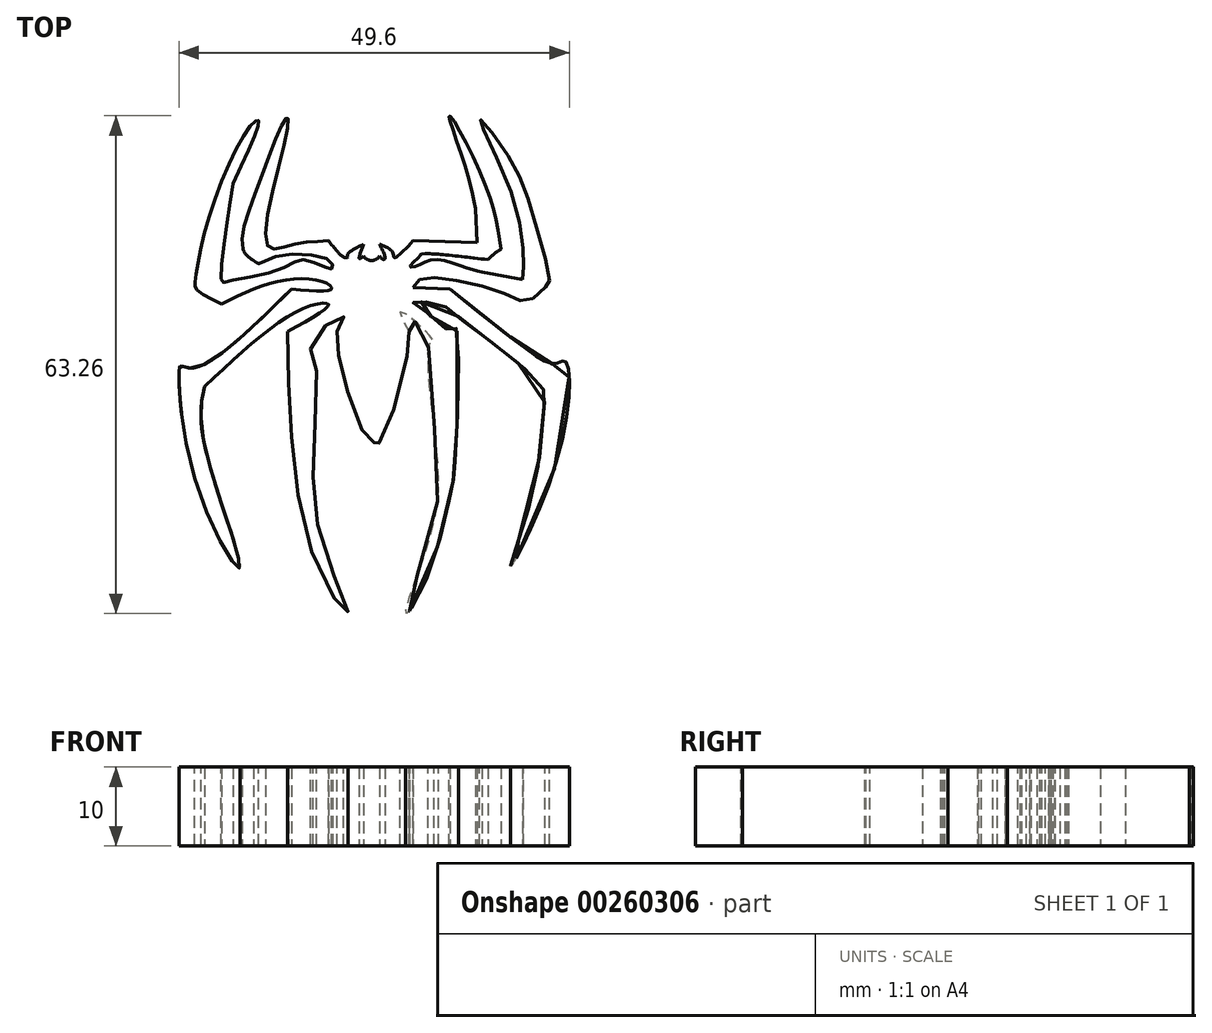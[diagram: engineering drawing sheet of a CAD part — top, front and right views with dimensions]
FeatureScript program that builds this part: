
annotation { "Feature Type Name" : "Feature", "Feature Type Description" : "" }
export const myFeature = defineFeature(function(context is Context, id is Id, definition is map)
    precondition{}
    {
        {
            var Q0;
            Q0=qCreatedBy(makeId("Top.planeOp"),FACE);
            var sketch = newSketch(context, id + "F0", { "sketchPlane" : qUnion([Q0])});
            skFitSpline(sketch, "E0", {"points": [v(26.14, 47.25) * mm, v(26.81, 45.39) * mm, v(26.49, 45.37) * mm, v(26.16, 45.74) * mm], "startDerivative": vector(2.32, -4.7) * mm, "endDerivative": vector(-1.04, 1.72) * mm});
            skFitSpline(sketch, "E1", {"points": [v(26.16, 45.74) * mm, v(25.6, 45.28) * mm, v(24.59, 45.3) * mm, v(24.1, 45.74) * mm], "startDerivative": vector(-1.46, -1.71) * mm, "endDerivative": vector(-1.26, 1.71) * mm});
            skFitSpline(sketch, "E2", {"points": [v(24.1, 45.74) * mm, v(23.56, 45.42) * mm, v(24.1, 47.25) * mm], "startDerivative": vector(-1.93, -1.58) * mm, "endDerivative": vector(1.61, 4.08) * mm});
            skFitSpline(sketch, "E3", {"points": [v(24.1, 47.25) * mm, v(22.13, 46.05) * mm, v(22.1, 45.6) * mm], "startDerivative": vector(-3.83, -1.81) * mm, "endDerivative": vector(0.37, -1.42) * mm});
            skFitSpline(sketch, "E4", {"points": [v(26.14, 47.25) * mm, v(27.79, 46.24) * mm, v(28, 45.57) * mm, v(30.4, 47.7) * mm], "startDerivative": vector(6.19, -2.42) * mm, "endDerivative": vector(7.2, 7.58) * mm});
            skFitSpline(sketch, "E5", {"points": [v(22.1, 45.6) * mm, v(21.6, 45.6) * mm, v(19.65, 47.7) * mm], "startDerivative": vector(-1.58, -0.44) * mm, "endDerivative": vector(-3.12, 4.02) * mm});
            skFitSpline(sketch, "E6", {"points": [v(30.4, 47.7) * mm, v(38.5, 47.45) * mm], "startDerivative": vector(8.09, -0.25) * mm, "endDerivative": vector(8.09, -0.25) * mm});
            skFitSpline(sketch, "E7", {"points": [v(38.5, 47.45) * mm, v(38.31, 51.77) * mm], "startDerivative": vector(-0.18, 4.33) * mm, "endDerivative": vector(-0.18, 4.33) * mm});
            skFitSpline(sketch, "E8", {"points": [v(38.31, 51.77) * mm, v(37.02, 57.13) * mm, v(35, 63.59) * mm, v(39.43, 55.13) * mm, v(41.56, 46.66) * mm], "startDerivative": vector(-3.78, 20.99) * mm, "endDerivative": vector(3.96, -27.47) * mm});
            skFitSpline(sketch, "E9", {"points": [v(41.56, 46.66) * mm, v(40.56, 45.93) * mm, v(39.9, 45.3) * mm], "startDerivative": vector(-1.98, -1.35) * mm, "endDerivative": vector(-1.33, -1.36) * mm});
            skFitSpline(sketch, "E10", {"points": [v(39.9, 45.3) * mm, v(31.39, 46) * mm, v(31.24, 45.74) * mm, v(30, 44.48) * mm, v(30.73, 44.43) * mm, v(33.04, 45.3) * mm, v(37.2, 44.25) * mm, v(39.13, 43.74) * mm], "startDerivative": vector(-44.14, 5.21) * mm, "endDerivative": vector(12.78, -2.6) * mm});
            skFitSpline(sketch, "E11", {"points": [v(39.13, 43.74) * mm, v(44.28, 42.76) * mm], "startDerivative": vector(5.15, -0.98) * mm, "endDerivative": vector(5.15, -0.98) * mm});
            skFitSpline(sketch, "E12", {"points": [v(44.28, 42.76) * mm, v(44.4, 45.3) * mm, v(42.57, 54.65) * mm, v(38.88, 63.08) * mm, v(42.44, 58.54) * mm, v(45.42, 51.6) * mm, v(47.74, 42.4) * mm, v(47.45, 42.05) * mm, v(45, 40.05) * mm, v(42.61, 40.75) * mm, v(35.3, 42.76) * mm, v(31.26, 42.76) * mm, v(30.4, 41.78) * mm], "startDerivative": vector(3.4, 35.7) * mm, "endDerivative": vector(-14.16, -25.9) * mm});
            skFitSpline(sketch, "E13", {"points": [v(30.4, 41.78) * mm, v(35.1, 41.55) * mm], "startDerivative": vector(4.7, -0.23) * mm, "endDerivative": vector(4.7, -0.23) * mm});
            skFitSpline(sketch, "E14", {"points": [v(35.1, 41.55) * mm, v(45.12, 33.68) * mm, v(48.54, 32.08) * mm, v(49.64, 32.42) * mm, v(49, 21.04) * mm, v(42.76, 6.35) * mm, v(45.7, 16.1) * mm, v(47, 26.53) * mm, v(46.76, 29.2) * mm, v(36.86, 37.45) * mm, v(33.48, 39.72) * mm, v(30.4, 39.88) * mm, v(31.15, 39.45) * mm, v(35.1, 36.36) * mm, v(35.82, 36.62) * mm, v(35.68, 19) * mm, v(35.41, 17.03) * mm, v(32.12, 4.73) * mm, v(29.47, 0.38) * mm, v(32.67, 10.5) * mm, v(33.34, 21.64) * mm, v(32.67, 34.85) * mm, v(33.04, 34.98) * mm, v(28.9, 38.7) * mm, v(29.89, 36.14) * mm], "startDerivative": vector(184.7, -149.72) * mm, "endDerivative": vector(82.13, -144.83) * mm});
            skFitSpline(sketch, "E15", {"points": [v(29.89, 36.14) * mm, v(29.6, 32.9) * mm, v(26.16, 22.03) * mm, v(25.72, 22.34) * mm, v(25.49, 22.53) * mm, v(25.37, 21.92) * mm, v(24.24, 23) * mm, v(21.4, 30.95) * mm, v(20.7, 35.26) * mm, v(21.09, 37.15) * mm, v(21.58, 38.06) * mm, v(20.26, 37.72) * mm, v(17.36, 34.15) * mm, v(17.78, 33.22) * mm, v(17.8, 21.56) * mm, v(18.95, 8.88) * mm, v(22.1, 0.38) * mm, v(18.78, 5.02) * mm, v(15.04, 21.56) * mm, v(14.44, 36.14) * mm], "startDerivative": vector(2.16, -48.8) * mm, "endDerivative": vector(-2.25, 149.18) * mm});
            skFitSpline(sketch, "E16", {"points": [v(14.44, 36.14) * mm, v(19.65, 39.59) * mm, v(16.6, 39.16) * mm, v(3.88, 29.17) * mm], "startDerivative": vector(26.34, 14.63) * mm, "endDerivative": vector(-28.05, -26.23) * mm});
            skFitSpline(sketch, "E17", {"points": [v(3.88, 29.17) * mm, v(3.88, 21.87) * mm, v(8.39, 6.18) * mm, v(3.04, 16.22) * mm, v(0.7, 31.56) * mm, v(0.89, 31.77) * mm, v(2.7, 31.58) * mm, v(14.94, 41.55) * mm], "startDerivative": vector(-8.49, -40.73) * mm, "endDerivative": vector(72.1, 71.44) * mm});
            skFitSpline(sketch, "E18", {"points": [v(14.94, 41.55) * mm, v(20.02, 41.55) * mm, v(19.65, 42.17) * mm, v(14.44, 42.76) * mm, v(6.05, 39.67) * mm], "startDerivative": vector(26.43, -2.35) * mm, "endDerivative": vector(-23.45, -11.45) * mm});
            skFitSpline(sketch, "E19", {"points": [v(6.05, 39.67) * mm, v(2.83, 41.55) * mm, v(2.7, 42.39) * mm, v(4.26, 49.98) * mm, v(9.6, 62.15) * mm, v(10.75, 62.99) * mm, v(7.52, 54.95) * mm], "startDerivative": vector(-29.06, 14.32) * mm, "endDerivative": vector(-24.24, -51.6) * mm});
            skFitSpline(sketch, "E20", {"points": [v(7.52, 54.95) * mm, v(6.86, 50.9) * mm, v(6.05, 42.5) * mm, v(6.55, 42.48) * mm, v(13.75, 44.16) * mm, v(16.52, 45.3) * mm, v(19.65, 44.16) * mm, v(20.17, 44.25) * mm, v(19.65, 45.3) * mm, v(12.46, 45.57) * mm, v(10.84, 44.8) * mm, v(8.78, 46.66) * mm], "startDerivative": vector(-5.12, -29.54) * mm, "endDerivative": vector(-26.59, 31.35) * mm});
            skFitSpline(sketch, "E21", {"points": [v(19.65, 47.7) * mm, v(14.78, 47.13) * mm, v(11.81, 47.23) * mm, v(14.52, 62.46) * mm, v(14.33, 63.34) * mm, v(10.84, 55.1) * mm, v(8.78, 46.66) * mm, v(10.84, 44.8) * mm], "startDerivative": vector(-36.1, -1.57) * mm, "endDerivative": vector(26, -13.56) * mm});
            skSolve(sketch);
        }
        {
            var Q0;
            Q0 = qSketchRegion(id + "F0", true);
            extrude(context, id + "F1", {"entities" : qUnion([Q0]), "depth" : 10 * mm});
        }
    });
